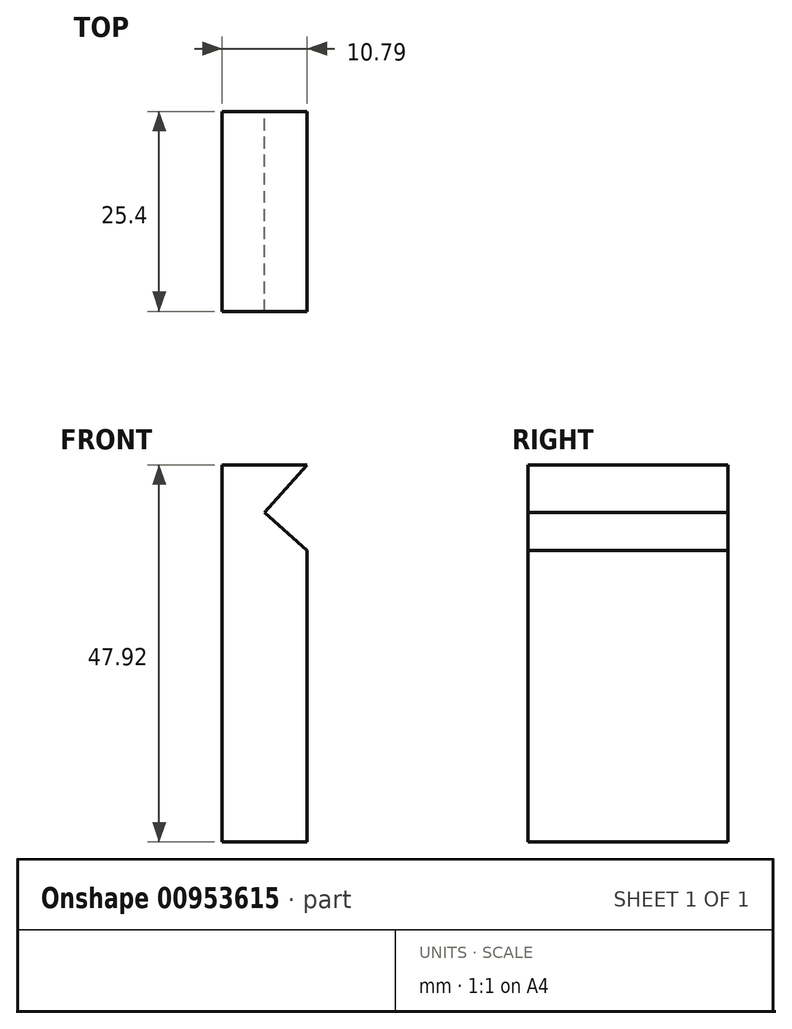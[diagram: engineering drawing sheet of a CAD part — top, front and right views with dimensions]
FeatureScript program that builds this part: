
annotation { "Feature Type Name" : "Feature", "Feature Type Description" : "" }
export const myFeature = defineFeature(function(context is Context, id is Id, definition is map)
    precondition{}
    {
        {
            var Q0;
            Q0=qCreatedBy(makeId("Front.planeOp"),FACE);
            var sketch = newSketch(context, id + "F0", { "sketchPlane" : qUnion([Q0])});
            skLineSegment(sketch, "E0", {"start": v(0, 0) * mm, "end": v(10.8, 0) * mm});
            skLineSegment(sketch, "E1", {"start": v(10.8, 0) * mm, "end": v(10.8, 47.92) * mm});
            skLineSegment(sketch, "E2", {"start": v(10.8, 47.92) * mm, "end": v(0, 47.92) * mm});
            skLineSegment(sketch, "E3", {"start": v(0, 0) * mm, "end": v(0, 47.92) * mm});
            skLineSegment(sketch, "E4", {"start": v(10.8, 47.92) * mm, "end": v(5.4, 41.88) * mm});
            skPoint(sketch, "E4.endSnap0", {"position": v(5.4, 47.92) * mm});
            skLineSegment(sketch, "E5", {"start": v(5.4, 41.88) * mm, "end": v(10.8, 37.06) * mm});
            skLineSegment(sketch, "E6", {"start": v(11.37, 36.7) * mm, "end": v(11.66, 47.92) * mm});
            skSolve(sketch);
        }
        {
            var Q0;
            Q0=makeQuery(id+"F0.imprint","IMPRINT",FACE,{"disambiguationData":[TD([[makeQuery(id+"F0.imprint","IMPRINT",EDGE,{"derivedFrom":sQuery(id+"F0.wireOp",EDGE,"E0")}),1.0]])]});
            extrude(context, id + "F1", {"entities" : qUnion([Q0]), "depth" : 25.4 * mm, "offsetDistance" : 25.4 * mm});
        }
    });
